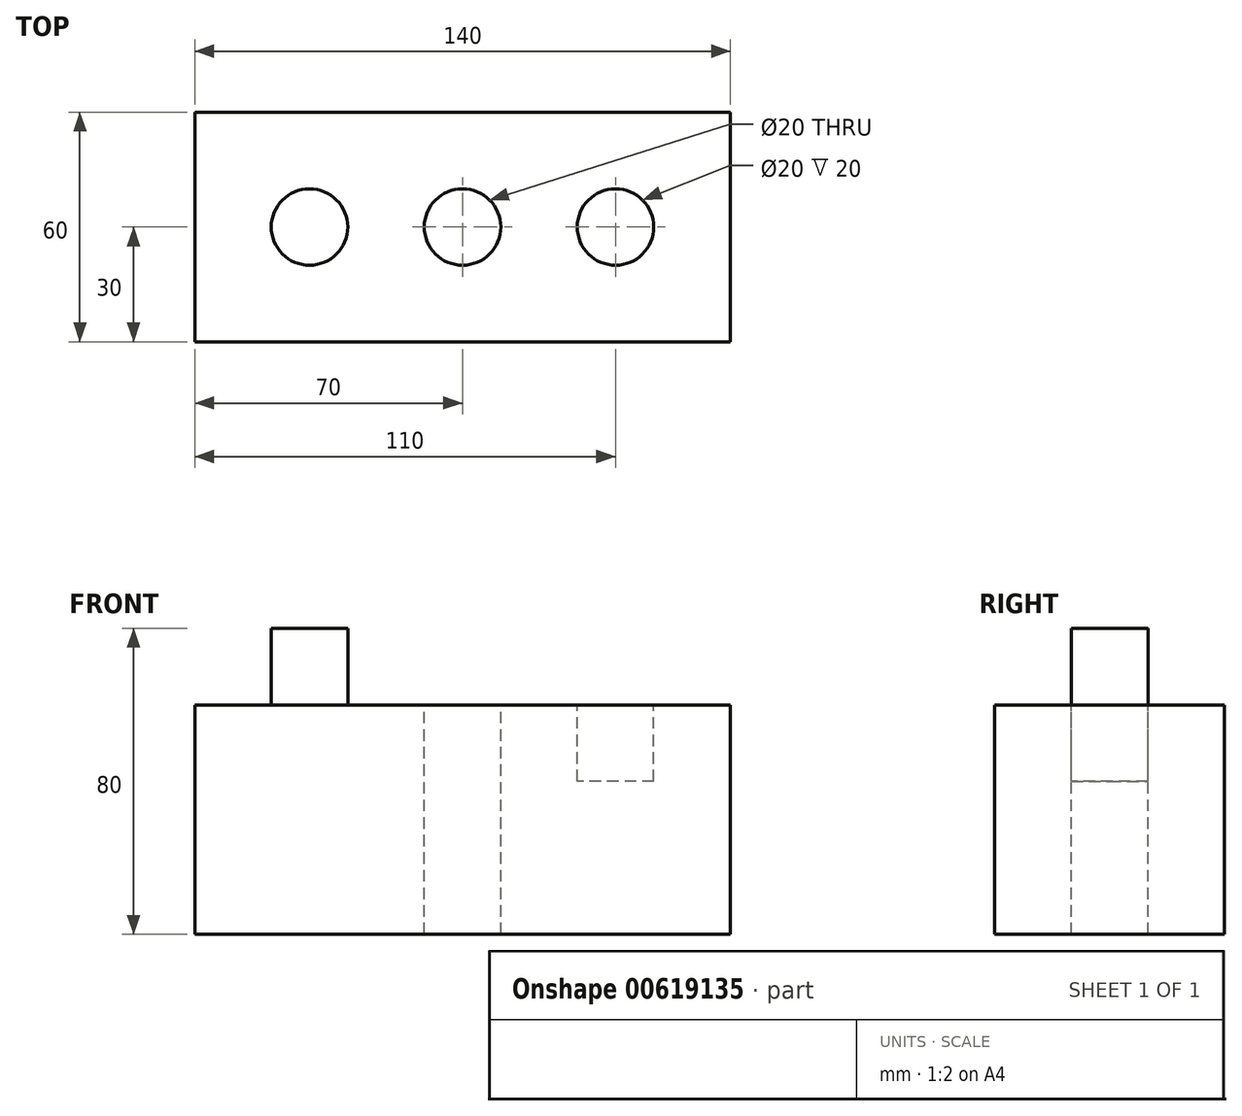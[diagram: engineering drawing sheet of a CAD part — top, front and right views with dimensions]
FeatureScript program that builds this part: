
annotation { "Feature Type Name" : "Feature", "Feature Type Description" : "" }
export const myFeature = defineFeature(function(context is Context, id is Id, definition is map)
    precondition{}
    {
        {
            var Q0;
            Q0=qCreatedBy(makeId("Front.planeOp"),FACE);
            var sketch = newSketch(context, id + "F0", { "sketchPlane" : qUnion([Q0])});
            skLineSegment(sketch, "E0.bottom", {"start": v(70, 30) * mm, "end": v(-70, 30) * mm});
            skLineSegment(sketch, "E0.top", {"start": v(70, -30) * mm, "end": v(-70, -30) * mm});
            skLineSegment(sketch, "E0.left", {"start": v(70, 30) * mm, "end": v(70, -30) * mm});
            skLineSegment(sketch, "E0.right", {"start": v(-70, 30) * mm, "end": v(-70, -30) * mm});
            skPoint(sketch, "E0.middle", {"position": v(0, 0) * mm});
            skSolve(sketch);
        }
        {
            var Q0;
            Q0=makeQuery(id+"F0.imprint","IMPRINT",FACE,{"disambiguationData":[TD([[makeQuery(id+"F0.imprint","IMPRINT",EDGE,{"derivedFrom":sQuery(id+"F0.wireOp",EDGE,"E0.bottom")}),1.0]])]});
            extrude(context, id + "F1", {"entities" : qUnion([Q0]), "depth" : 60 * mm, "offsetDistance" : 25 * mm});
        }
        {
            var Q0;
            Q0=makeQuery(id+"F1.opExtrude","SWEPT_FACE",FACE,{"disambiguationData":[OSD([sQuery(id+"F0.wireOp",EDGE,"E0.bottom")])]});
            var sketch = newSketch(context, id + "F2", { "sketchPlane" : qUnion([Q0])});
            skCircle(sketch, "E1", {"center": v(-40, -30) * mm, "radius": 10 * mm});
            skSolve(sketch);
        }
        {
            var Q0;
            Q0=makeQuery(id+"F2.imprint","IMPRINT",FACE,{"disambiguationData":[TD([[makeQuery(id+"F2.imprint","IMPRINT",EDGE,{"derivedFrom":sQuery(id+"F2.wireOp",EDGE,"E1")}),1.0]])]});
            extrude(context, id + "F3", {"entities" : qUnion([Q0]), "operationType" : NewBodyOperationType.ADD, "depth" : 20 * mm, "offsetDistance" : 25 * mm});
        }
        {
            var Q0;
            Q0=makeQuery(id+"F1.opExtrude","SWEPT_FACE",FACE,{"disambiguationData":[OSD([sQuery(id+"F0.wireOp",EDGE,"E0.bottom")])]});
            var sketch = newSketch(context, id + "F4", { "sketchPlane" : qUnion([Q0])});
            skCircle(sketch, "E2", {"center": v(0, -30) * mm, "radius": 10 * mm});
            skSolve(sketch);
        }
        {
            var Q0;
            Q0 = qSketchRegion(id + "F4", true);
            extrude(context, id + "F5", {"entities" : qUnion([Q0]), "operationType" : NewBodyOperationType.REMOVE, "oppositeDirection" : true, "depth" : 65 * mm, "offsetDistance" : 25 * mm});
        }
        {
            var Q0;
            Q0=makeQuery(id+"F2.imprint","IMPRINT",FACE,{"disambiguationData":[TD([[makeQuery(id+"F2.imprint","IMPRINT",EDGE,{"derivedFrom":sQuery(id+"F2.wireOp",EDGE,"E1")}),-1.0]])]});
            var sketch = newSketch(context, id + "F6", { "sketchPlane" : qUnion([Q0])});
            skCircle(sketch, "E3", {"center": v(40, -30) * mm, "radius": 10 * mm});
            skSolve(sketch);
        }
        {
            var Q0;
            Q0 = qSketchRegion(id + "F6", true);
            extrude(context, id + "F7", {"entities" : qUnion([Q0]), "operationType" : NewBodyOperationType.REMOVE, "oppositeDirection" : true, "depth" : 20 * mm, "offsetDistance" : 25 * mm});
        }
    });
